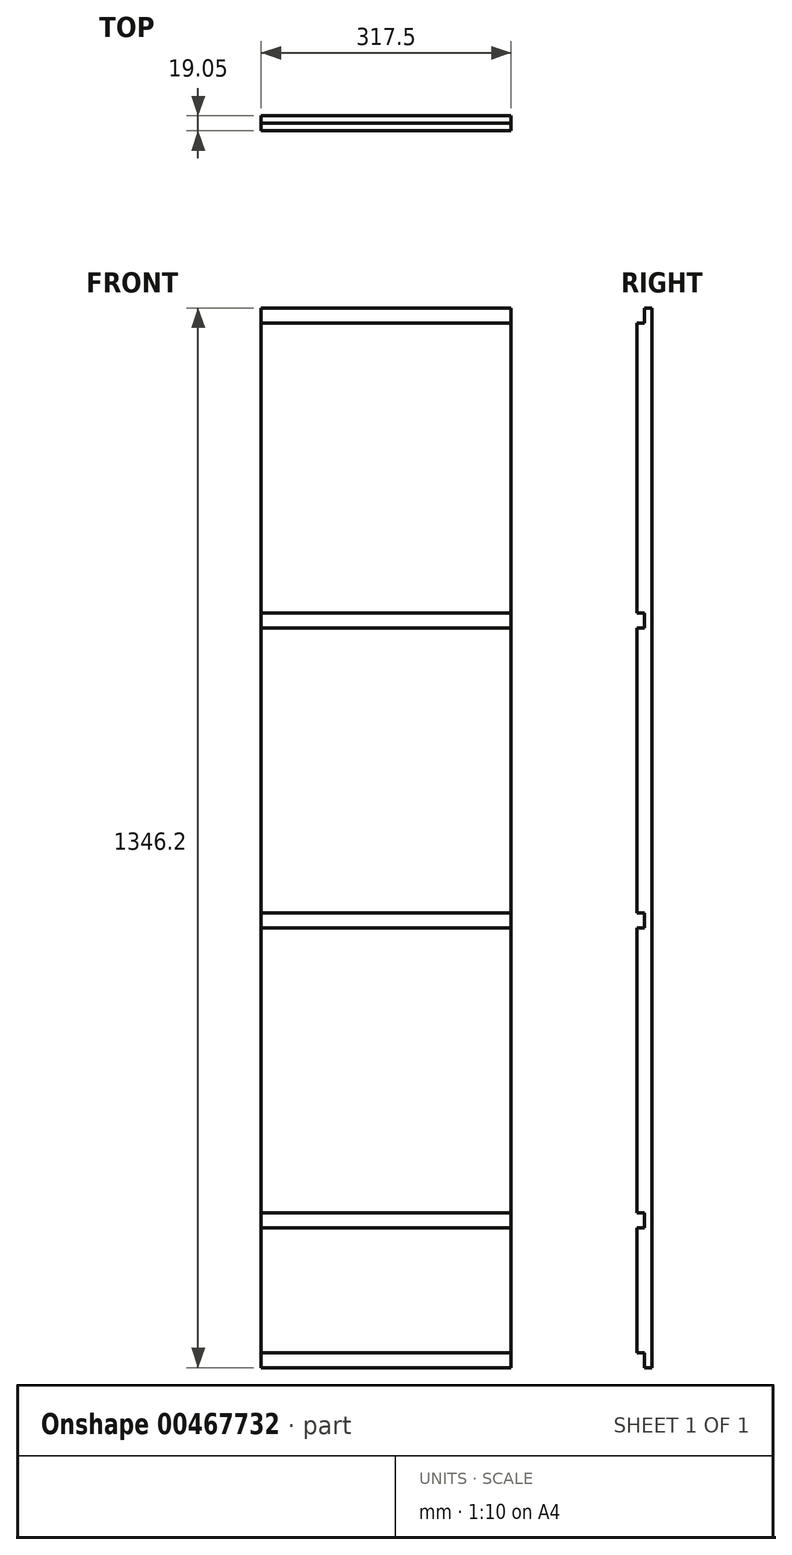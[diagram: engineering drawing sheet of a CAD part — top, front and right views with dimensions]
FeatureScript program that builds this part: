
annotation { "Feature Type Name" : "Feature", "Feature Type Description" : "" }
export const myFeature = defineFeature(function(context is Context, id is Id, definition is map)
    precondition{}
    {
        {
            var Q0;
            Q0=qCreatedBy(makeId("Front.planeOp"),FACE);
            var sketch = newSketch(context, id + "F0", { "sketchPlane" : qUnion([Q0])});
            skLineSegment(sketch, "E0.bottom", {"start": v(0, 0) * mm, "end": v(317.5, 0) * mm});
            skLineSegment(sketch, "E0.top", {"start": v(0, 1346.2) * mm, "end": v(317.5, 1346.2) * mm});
            skLineSegment(sketch, "E0.left", {"start": v(0, 0) * mm, "end": v(0, 1346.2) * mm});
            skLineSegment(sketch, "E0.right", {"start": v(317.5, 0) * mm, "end": v(317.5, 1346.2) * mm});
            skSolve(sketch);
        }
        {
            var Q0;
            Q0 = qSketchRegion(id + "F0", true);
            extrude(context, id + "F1", {"entities" : qUnion([Q0]), "depth" : 19.05 * mm});
        }
        {
            var Q0;
            Q0=makeQuery(id+"F1.opExtrude","SWEPT_FACE",FACE,{"disambiguationData":[OSD([sQuery(id+"F0.wireOp",EDGE,"E0.top")])]});
            var sketch = newSketch(context, id + "F2", { "sketchPlane" : qUnion([Q0])});
            skLineSegment(sketch, "E1.bottom", {"start": v(0, -9.53) * mm, "end": v(317.5, -9.53) * mm});
            skLineSegment(sketch, "E1.top", {"start": v(0, -19.05) * mm, "end": v(317.5, -19.05) * mm});
            skLineSegment(sketch, "E1.left", {"start": v(0, -9.53) * mm, "end": v(0, -19.05) * mm});
            skLineSegment(sketch, "E1.right", {"start": v(317.5, -9.53) * mm, "end": v(317.5, -19.05) * mm});
            skSolve(sketch);
        }
        {
            var Q0;
            Q0=makeQuery(id+"F2.imprint","IMPRINT",FACE,{"disambiguationData":[TD([[makeQuery(id+"F2.imprint","IMPRINT",EDGE,{"derivedFrom":sQuery(id+"F2.wireOp",EDGE,"E1.bottom")}),-1.0]])]});
            extrude(context, id + "F3", {"entities" : qUnion([Q0]), "operationType" : NewBodyOperationType.REMOVE, "oppositeDirection" : true, "depth" : 19.05 * mm});
        }
        {
            var Q0;
            Q0=makeQuery(id+"F1.opExtrude","SWEPT_FACE",FACE,{"disambiguationData":[OSD([sQuery(id+"F0.wireOp",EDGE,"E0.bottom")])]});
            var sketch = newSketch(context, id + "F4", { "sketchPlane" : qUnion([Q0])});
            skLineSegment(sketch, "E2.bottom", {"start": v(0, 9.53) * mm, "end": v(317.5, 9.53) * mm});
            skLineSegment(sketch, "E2.top", {"start": v(0, 19.05) * mm, "end": v(317.5, 19.05) * mm});
            skLineSegment(sketch, "E2.left", {"start": v(0, 9.53) * mm, "end": v(0, 19.05) * mm});
            skLineSegment(sketch, "E2.right", {"start": v(317.5, 9.53) * mm, "end": v(317.5, 19.05) * mm});
            skSolve(sketch);
        }
        {
            var Q0;
            Q0 = qSketchRegion(id + "F4", true);
            extrude(context, id + "F5", {"entities" : qUnion([Q0]), "operationType" : NewBodyOperationType.REMOVE, "oppositeDirection" : true, "depth" : 19.05 * mm});
        }
        {
            var Q0;
            Q0=makeQuery(id+"F1.opExtrude","CAP_FACE",FACE,{"disambiguationData":[OSD([sQuery(id+"F0.wireOp",EDGE,"E0.bottom"),sQuery(id+"F0.wireOp",EDGE,"E0.top"),sQuery(id+"F0.wireOp",EDGE,"E0.left"),sQuery(id+"F0.wireOp",EDGE,"E0.right")])],"isStart":false});
            var sketch = newSketch(context, id + "F6", { "sketchPlane" : qUnion([Q0])});
            skLineSegment(sketch, "E3.bottom", {"start": v(0, 177.8) * mm, "end": v(317.5, 177.8) * mm});
            skLineSegment(sketch, "E3.top", {"start": v(0, 196.85) * mm, "end": v(317.5, 196.85) * mm});
            skLineSegment(sketch, "E3.left", {"start": v(0, 177.8) * mm, "end": v(0, 196.85) * mm});
            skLineSegment(sketch, "E3.right", {"start": v(317.5, 177.8) * mm, "end": v(317.5, 196.85) * mm});
            skSolve(sketch);
        }
        {
            var Q0;
            Q0=makeQuery(id+"F6.imprint","IMPRINT",FACE,{"disambiguationData":[TD([[makeQuery(id+"F6.imprint","IMPRINT",EDGE,{"derivedFrom":sQuery(id+"F6.wireOp",EDGE,"E3.bottom")}),1.0]])]});
            extrude(context, id + "F7", {"entities" : qUnion([Q0]), "operationType" : NewBodyOperationType.REMOVE, "oppositeDirection" : true, "depth" : 9.52 * mm});
        }
        {
            var Q0;
            {var subQ0=sQuery(id+"F0.wireOp",EDGE,"E0.left");var subQ1=sQuery(id+"F0.wireOp",EDGE,"E0.right");Q0=makeQuery(id+"F7.boolean.opBoolean","SPLIT",FACE,{"disambiguationData":[TD([makeQuery(id+"F7.opExtrude","SWEPT_FACE",FACE,{"disambiguationData":[OSD([sQuery(id+"F6.wireOp",EDGE,"E3.top")])]})])],"derivedFrom":makeQuery(id+"F1.opExtrude","CAP_FACE",FACE,{"disambiguationData":[OSD([sQuery(id+"F0.wireOp",EDGE,"E0.bottom"),sQuery(id+"F0.wireOp",EDGE,"E0.top"),subQ0,subQ1])],"isStart":false})});}
            var sketch = newSketch(context, id + "F8", { "sketchPlane" : qUnion([Q0])});
            skLineSegment(sketch, "E4.bottom", {"start": v(0, 558.8) * mm, "end": v(317.5, 558.8) * mm});
            skLineSegment(sketch, "E4.top", {"start": v(0, 577.85) * mm, "end": v(317.5, 577.85) * mm});
            skLineSegment(sketch, "E4.left", {"start": v(0, 558.8) * mm, "end": v(0, 577.85) * mm});
            skLineSegment(sketch, "E4.right", {"start": v(317.5, 558.8) * mm, "end": v(317.5, 577.85) * mm});
            skSolve(sketch);
        }
        {
            var Q0;
            Q0=makeQuery(id+"F8.imprint","IMPRINT",FACE,{"disambiguationData":[TD([[makeQuery(id+"F8.imprint","IMPRINT",EDGE,{"derivedFrom":sQuery(id+"F8.wireOp",EDGE,"E4.bottom")}),1.0]])]});
            extrude(context, id + "F9", {"entities" : qUnion([Q0]), "operationType" : NewBodyOperationType.REMOVE, "oppositeDirection" : true, "depth" : 9.52 * mm});
        }
        {
            var Q0;
            {var subQ0=sQuery(id+"F0.wireOp",EDGE,"E0.left");var subQ2=sQuery(id+"F0.wireOp",EDGE,"E0.right");Q0=makeQuery(id+"F9.boolean.opBoolean","SPLIT",FACE,{"disambiguationData":[TD([makeQuery(id+"F9.opExtrude","SWEPT_FACE",FACE,{"disambiguationData":[OSD([sQuery(id+"F8.wireOp",EDGE,"E4.top")])]})])],"derivedFrom":makeQuery(id+"F7.boolean.opBoolean","SPLIT",FACE,{"disambiguationData":[TD([makeQuery(id+"F7.opExtrude","SWEPT_FACE",FACE,{"disambiguationData":[OSD([sQuery(id+"F6.wireOp",EDGE,"E3.top")])]})])],"derivedFrom":makeQuery(id+"F1.opExtrude","CAP_FACE",FACE,{"disambiguationData":[OSD([sQuery(id+"F0.wireOp",EDGE,"E0.bottom"),sQuery(id+"F0.wireOp",EDGE,"E0.top"),subQ0,subQ2])],"isStart":false})})});}
            var sketch = newSketch(context, id + "F10", { "sketchPlane" : qUnion([Q0])});
            skLineSegment(sketch, "E5.bottom", {"start": v(0, 958.85) * mm, "end": v(317.5, 958.85) * mm});
            skLineSegment(sketch, "E5.top", {"start": v(0, 939.8) * mm, "end": v(317.5, 939.8) * mm});
            skLineSegment(sketch, "E5.left", {"start": v(0, 958.85) * mm, "end": v(0, 939.8) * mm});
            skLineSegment(sketch, "E5.right", {"start": v(317.5, 958.85) * mm, "end": v(317.5, 939.8) * mm});
            skSolve(sketch);
        }
        {
            var Q0;
            Q0=makeQuery(id+"F10.imprint","IMPRINT",FACE,{"disambiguationData":[TD([[makeQuery(id+"F10.imprint","IMPRINT",EDGE,{"derivedFrom":sQuery(id+"F10.wireOp",EDGE,"E5.bottom")}),-1.0]])]});
            extrude(context, id + "F11", {"entities" : qUnion([Q0]), "operationType" : NewBodyOperationType.REMOVE, "oppositeDirection" : true, "depth" : 9.52 * mm});
        }
    });
